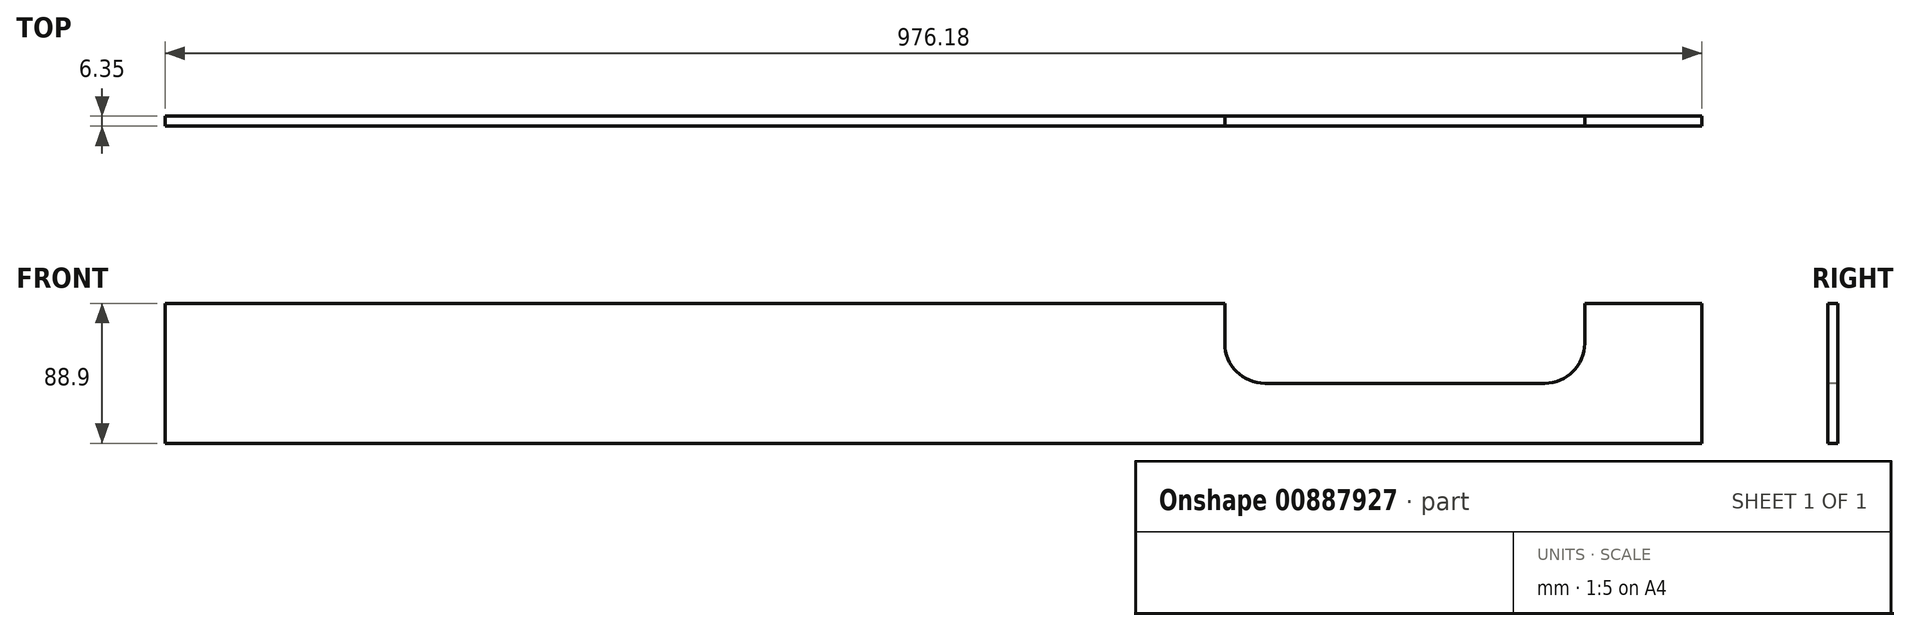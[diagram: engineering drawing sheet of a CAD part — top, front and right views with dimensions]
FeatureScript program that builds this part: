
annotation { "Feature Type Name" : "Feature", "Feature Type Description" : "" }
export const myFeature = defineFeature(function(context is Context, id is Id, definition is map)
    precondition{}
    {
        {
            var Q0;
            Q0=qCreatedBy(makeId("Front.planeOp"),FACE);
            var sketch = newSketch(context, id + "F0", { "sketchPlane" : qUnion([Q0])});
            skLineSegment(sketch, "E0.bottom", {"start": v(0, 0) * mm, "end": v(2438.4, 0) * mm});
            skLineSegment(sketch, "E0.top", {"start": v(0, 88.9) * mm, "end": v(2438.4, 88.9) * mm});
            skLineSegment(sketch, "E0.left", {"start": v(0, 0) * mm, "end": v(0, 88.9) * mm});
            skLineSegment(sketch, "E0.right", {"start": v(2438.4, 0) * mm, "end": v(2438.4, 88.9) * mm});
            skSolve(sketch);
        }
        {
            var Q0;
            Q0 = qSketchRegion(id + "F0", true);
            extrude(context, id + "F1", {"entities" : qUnion([Q0]), "depth" : 6.35 * mm, "offsetDistance" : 25.4 * mm});
        }
        {
            var Q0;
            Q0=makeQuery(id+"F1.opExtrude","CAP_FACE",FACE,{"disambiguationData":[OSD([sQuery(id+"F0.wireOp",EDGE,"E0.bottom"),sQuery(id+"F0.wireOp",EDGE,"E0.top"),sQuery(id+"F0.wireOp",EDGE,"E0.left"),sQuery(id+"F0.wireOp",EDGE,"E0.right")])],"isStart":false});
            var sketch = newSketch(context, id + "F2", { "sketchPlane" : qUnion([Q0])});
            skLineSegment(sketch, "E1", {"start": v(1219.2, 88.9) * mm, "end": v(1219.2, 0) * mm, "construction": true});
            skLineSegment(sketch, "E2", {"start": v(673.1, 88.9) * mm, "end": v(673.1, 38.1) * mm});
            skLineSegment(sketch, "E3", {"start": v(673.1, 38.1) * mm, "end": v(787.4, 38.1) * mm});
            skLineSegment(sketch, "E4", {"start": v(787.4, 38.1) * mm, "end": v(901.7, 38.1) * mm});
            skLineSegment(sketch, "E5", {"start": v(901.7, 38.1) * mm, "end": v(901.7, 88.9) * mm});
            skSolve(sketch);
        }
        {
            var Q0;
            Q0 = qSketchRegion(id + "F2", true);
            var Q1;
            {var subQ1=sQuery(id+"F2.wireOp",EDGE,"E2");Q1=makeQuery(id+"F2.imprint","IMPRINT",FACE,{"disambiguationData":[TD([[makeQuery(id+"F2.imprint","IMPRINT",EDGE,{"derivedFrom":subQ1}),1.0]])]});}
            extrude(context, id + "F3", {"entities" : qUnion([Q0, Q1]), "operationType" : NewBodyOperationType.REMOVE, "endBound" : BoundingType.THROUGH_ALL, "oppositeDirection" : true, "depth" : 25.4 * mm, "offsetDistance" : 25.4 * mm});
        }
        {
            var Q0;
            Q0=makeQuery(id+"F3.boolean.opBoolean","COPY",EDGE,{"derivedFrom":makeQuery(id+"F3.opExtrude","SWEPT_EDGE",EDGE,{"disambiguationData":[OSD([sQuery(id+"F2.wireOp",EDGE,"E2"),sQuery(id+"F2.wireOp",EDGE,"E3")])]})});
            var Q1;
            Q1=makeQuery(id+"F3.boolean.opBoolean","COPY",EDGE,{"derivedFrom":makeQuery(id+"F3.opExtrude","SWEPT_EDGE",EDGE,{"disambiguationData":[OSD([sQuery(id+"F2.wireOp",EDGE,"E4"),sQuery(id+"F2.wireOp",EDGE,"E5")])]})});
            fillet(context, id + "F4", {"entities" : qUnion([Q0, Q1]), "radius" : 25.4 * mm, "tangentPropagation" : true, "allowEdgeOverflow" : false});
        }
        {
            var Q0;
            Q0=makeQuery(id+"F1.opExtrude","CAP_FACE",FACE,{"disambiguationData":[OSD([sQuery(id+"F0.wireOp",EDGE,"E0.bottom"),sQuery(id+"F0.wireOp",EDGE,"E0.top"),sQuery(id+"F0.wireOp",EDGE,"E0.left"),sQuery(id+"F0.wireOp",EDGE,"E0.right")])],"isStart":false});
            var sketch = newSketch(context, id + "F5", { "sketchPlane" : qUnion([Q0])});
            skLineSegment(sketch, "E6", {"start": v(976.18, 88.9) * mm, "end": v(976.18, 0) * mm});
            skSolve(sketch);
        }
        {
            var Q0;
            Q0 = qSketchRegion(id + "F5", true);
            var Q1;
            {var subQ0=sQuery(id+"F5.wireOp",EDGE,"E6");Q1=makeQuery(id+"F5.imprint","IMPRINT",FACE,{"disambiguationData":[TD([[makeQuery(id+"F5.imprint","IMPRINT",EDGE,{"derivedFrom":subQ0}),1.0]])]});}
            extrude(context, id + "F6", {"entities" : qUnion([Q0, Q1]), "operationType" : NewBodyOperationType.REMOVE, "endBound" : BoundingType.THROUGH_ALL, "oppositeDirection" : true, "depth" : 25.4 * mm, "offsetDistance" : 25.4 * mm});
        }
    });
